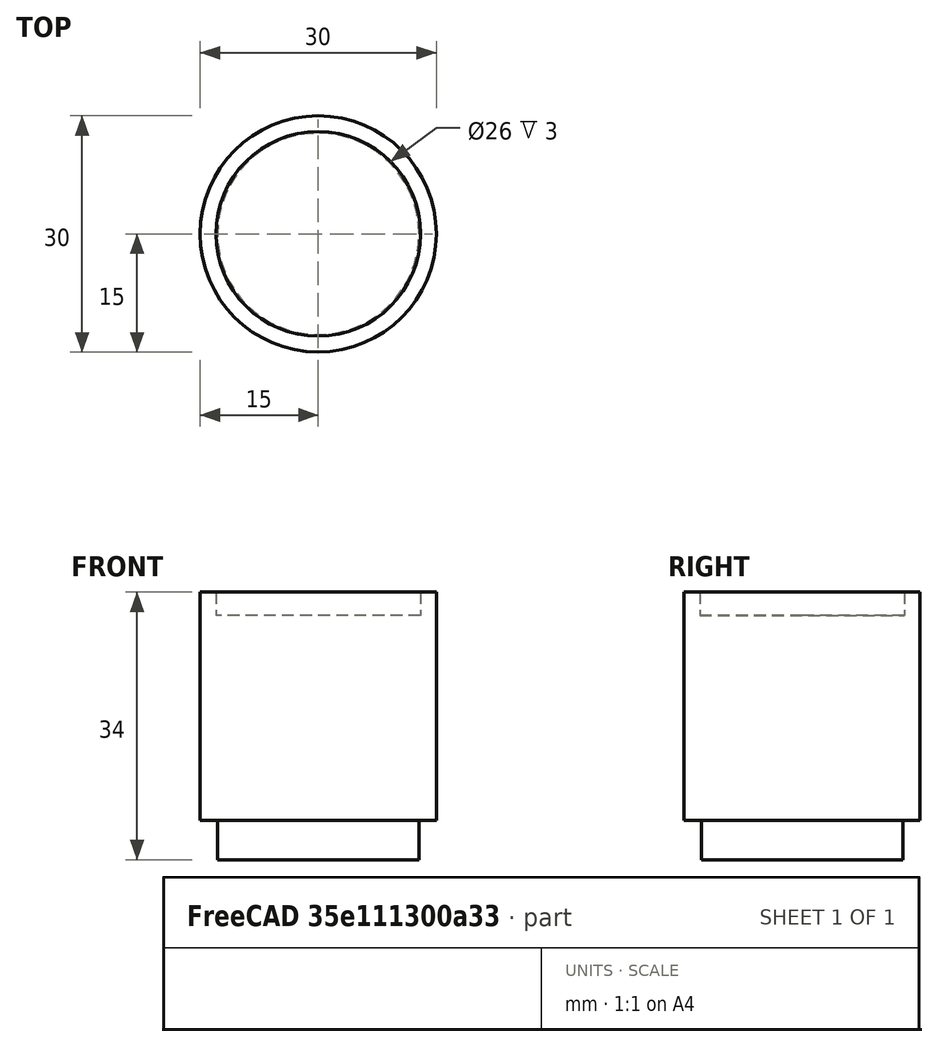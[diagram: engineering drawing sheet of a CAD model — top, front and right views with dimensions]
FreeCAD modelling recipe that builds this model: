
FCSTD DOCUMENT  (FreeCAD 1.0R39319 (Git))
Label: Lens_PT361060M3MP12
License: All rights reserved
LicenseURL: https://en.wikipedia.org/wiki/All_rights_reserved
objects: Sketcher::SketchObject×1, PartDesign::Revolution×1, PartDesign::Body×1, PartDesign::CoordinateSystem×1, App::Part×1
note: 7 computed .brp shape members not serialized (recipe doc carries the construction recipe); baked Part::Feature solids carry a one-line shape summary decoded from their .brp

FEATURE [Sketcher::SketchObject] Sketch
  ArcFitTolerance = 1e-06
  AttachmentSupport = -> [XZ_Plane001]
  FullyConstrained = true
  MakeInternals = false
  MapMode = 5
  Placement = pos=(0,0,0) rot=(1,0,0;1.5708rad)
  sketch-geometry (8):
    g0: LineSegment StartX=0 StartY=0 StartZ=0 EndX=12.8 EndY=0 EndZ=0
    g1: LineSegment StartX=12.8 StartY=0 StartZ=0 EndX=12.8 EndY=5 EndZ=0
    g2: LineSegment StartX=12.8 StartY=5 StartZ=0 EndX=15 EndY=5 EndZ=0
    g3: LineSegment StartX=15 StartY=5 StartZ=0 EndX=15 EndY=34 EndZ=0
    g4: LineSegment StartX=15 StartY=34 StartZ=0 EndX=13 EndY=34 EndZ=0
    g5: LineSegment StartX=13 StartY=34 StartZ=0 EndX=13 EndY=31 EndZ=0
    g6: LineSegment StartX=13 StartY=31 StartZ=0 EndX=0 EndY=31 EndZ=0
    g7: LineSegment StartX=0 StartY=31 StartZ=0 EndX=0 EndY=0 EndZ=0
  constraints (24):
    c: PointOnObject(g0,g-2)
    c: Horizontal(g0)
    c: Coincident(g0,g1)
    c: Vertical(g1)
    c: Coincident(g1,g2)
    c: Horizontal(g2)
    c: Coincident(g2,g3)
    c: Vertical(g3)
    c: Coincident(g3,g4)
    c: Coincident(g4,g5)
    c: Vertical(g5)
    c: Coincident(g5,g6)
    c: Horizontal(g6)
    c: Coincident(g6,g7)
    c: Coincident(g7,g0)
    c: Vertical(g7)
    c: Distance(g7,g1) = 12.8
    c: Distance(g7,g3) = 15
    c: Horizontal(g4)
    c: Distance(g0,g4) = 34
    c: Distance(g0,g2) = 5
    c: Distance(g-2,g5) = 13
    c: Distance(g4,g6) = 3
    c: PointOnObject(g0,g-1)
FEATURE [PartDesign::Revolution] Revolution
  Angle = 360
  Angle2 = 60
  Axis = (0,2e-16,1)
  Base = (0,0,0)
  Placement = pos=(0,0,0) rot=(1,0,0;1.5708rad)
  Profile = -> Sketch
  ReferenceAxis = -> Sketch [V_Axis]
  Refine = true
  Reversed = true
  Suppressed = false
  Type = 0
FEATURE [PartDesign::Body] Body  label="Lens_PT361060M3MP1201"
  AllowCompound = false
  Group = -> [Sketch,Revolution]
  Origin = -> Origin001
  Tip = -> Revolution
FEATURE [PartDesign::CoordinateSystem] LCS_1
  AttacherType = Attacher::AttachEngine3D
  AttachmentSupport = -> [Revolution]
  MapMode = 11
  Placement = pos=(-1.8e-15,2.2e-15,5) rot=(0.707107,-0.707107,0;3.14159rad)
FEATURE [App::Part] Part  label="Lens_PT361060M3MP12"
  Group = -> [Body,LCS_1]
  Origin = -> Origin
